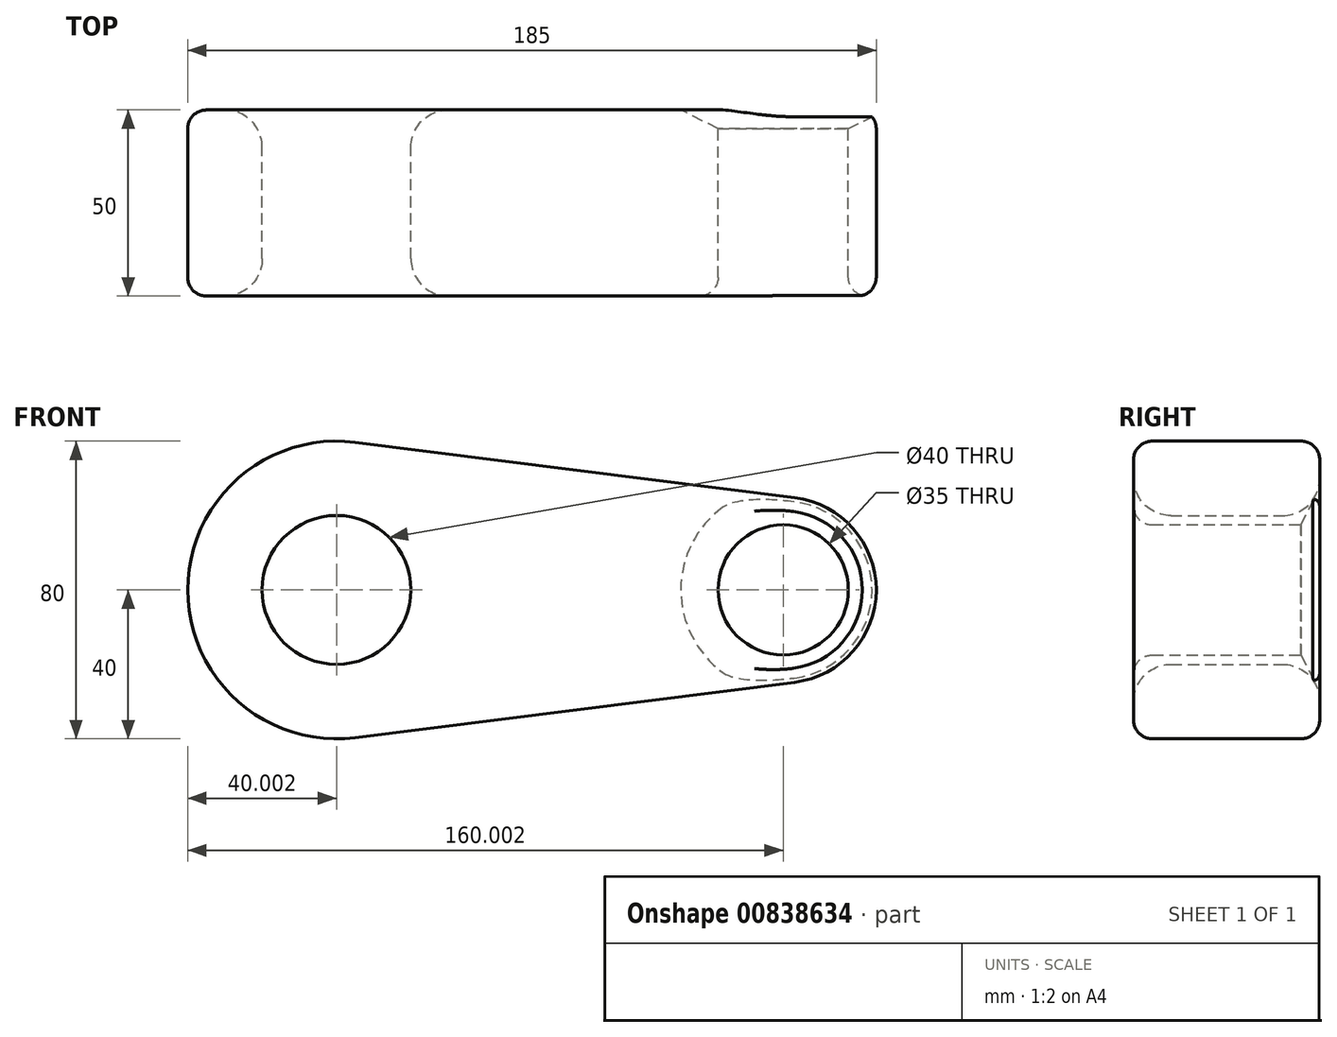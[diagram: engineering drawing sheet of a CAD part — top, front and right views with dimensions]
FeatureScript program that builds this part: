
annotation { "Feature Type Name" : "Feature", "Feature Type Description" : "" }
export const myFeature = defineFeature(function(context is Context, id is Id, definition is map)
    precondition{}
    {
        {
            var Q0;
            Q0=qCreatedBy(makeId("Front.planeOp"),FACE);
            var sketch = newSketch(context, id + "F0", { "sketchPlane" : qUnion([Q0])});
            skCircle(sketch, "E0", {"center": v(-83.9, 0) * mm, "radius": 40 * mm});
            skCircle(sketch, "E1", {"center": v(36.1, 0) * mm, "radius": 25 * mm});
            skLineSegment(sketch, "E2", {"start": v(-78.9, 39.69) * mm, "end": v(39.22, 24.8) * mm});
            skLineSegment(sketch, "E3", {"start": v(-78.9, -39.69) * mm, "end": v(39.22, -24.8) * mm});
            skCircle(sketch, "E4", {"center": v(-83.9, 0) * mm, "radius": 20 * mm});
            skCircle(sketch, "E5", {"center": v(36.1, 0) * mm, "radius": 17.5 * mm});
            skSolve(sketch);
        }
        {
            var Q0;
            Q0 = qSketchRegion(id + "F0", true);
            extrude(context, id + "F1", {"entities" : qUnion([Q0]), "depth" : 25 * mm, "offsetDistance" : 25 * mm});
        }
        {
            var Q0;
            Q0 = qSketchRegion(id + "F0", true);
            extrude(context, id + "F2", {"entities" : qUnion([Q0]), "operationType" : NewBodyOperationType.ADD, "depth" : 50 * mm, "offsetDistance" : 25 * mm});
        }
        {
            var Q0;
            {var subQ0=sQuery(id+"F0.wireOp",EDGE,"E4");Q0=makeQuery(id+"F2.boolean.opBoolean","MERGE",FACE,{"derivedFrom":[makeQuery(id+"F1.opExtrude","SWEPT_FACE",FACE,{"disambiguationData":[OSD([subQ0])]}),makeQuery(id+"F2.opExtrude","SWEPT_FACE",FACE,{"disambiguationData":[OSD([subQ0])]})]});}
            fillet(context, id + "F3", {"entities" : qUnion([Q0]), "radius" : 10 * mm, "tangentPropagation" : true, "allowEdgeOverflow" : false});
        }
        {
            var Q0;
            {var subQ0=sQuery(id+"F0.wireOp",EDGE,"E3");Q0=makeQuery(id+"F2.boolean.opBoolean","MERGE",FACE,{"derivedFrom":[makeQuery(id+"F1.opExtrude","SWEPT_FACE",FACE,{"disambiguationData":[OSD([subQ0])]}),makeQuery(id+"F2.opExtrude","SWEPT_FACE",FACE,{"disambiguationData":[OSD([subQ0])]})]});}
            var Q1;
            Q1=makeQuery(id+"F2.opExtrude","CAP_FACE",FACE,{"disambiguationData":[OSD([sQuery(id+"F0.wireOp",EDGE,"E0"),sQuery(id+"F0.wireOp",EDGE,"E1"),sQuery(id+"F0.wireOp",EDGE,"E2"),sQuery(id+"F0.wireOp",EDGE,"E3"),sQuery(id+"F0.wireOp",EDGE,"E4"),sQuery(id+"F0.wireOp",EDGE,"E5")])],"isStart":false});
            fillet(context, id + "F4", {"entities" : qUnion([Q0, Q1]), "radius" : 5 * mm, "tangentPropagation" : true, "allowEdgeOverflow" : false});
        }
        {
            var Q0;
            {var subQ0=sQuery(id+"F0.wireOp",EDGE,"E5");Q0=makeQuery(id+"F2.boolean.opBoolean","MERGE",FACE,{"derivedFrom":[makeQuery(id+"F1.opExtrude","SWEPT_FACE",FACE,{"disambiguationData":[OSD([subQ0])]}),makeQuery(id+"F2.opExtrude","SWEPT_FACE",FACE,{"disambiguationData":[OSD([subQ0])]})]});}
            var Q1;
            {var subQ0=sQuery(id+"F0.wireOp",EDGE,"E3");Q1=makeQuery(id+"F2.boolean.opBoolean","MERGE",FACE,{"derivedFrom":[makeQuery(id+"F1.opExtrude","SWEPT_FACE",FACE,{"disambiguationData":[OSD([subQ0])]}),makeQuery(id+"F2.opExtrude","SWEPT_FACE",FACE,{"disambiguationData":[OSD([subQ0])]})]});}
            var Q2;
            {var subQ0=sQuery(id+"F0.wireOp",EDGE,"E0");Q2=makeQuery(id+"F2.boolean.opBoolean","MERGE",FACE,{"derivedFrom":[makeQuery(id+"F1.opExtrude","SWEPT_FACE",FACE,{"disambiguationData":[OSD([subQ0])]}),makeQuery(id+"F2.opExtrude","SWEPT_FACE",FACE,{"disambiguationData":[OSD([subQ0])]})]});}
            var Q3;
            Q3=makeQuery(id+"F2.opExtrude","CAP_FACE",FACE,{"disambiguationData":[OSD([sQuery(id+"F0.wireOp",EDGE,"E0"),sQuery(id+"F0.wireOp",EDGE,"E1"),sQuery(id+"F0.wireOp",EDGE,"E2"),sQuery(id+"F0.wireOp",EDGE,"E3"),sQuery(id+"F0.wireOp",EDGE,"E4"),sQuery(id+"F0.wireOp",EDGE,"E5")])],"isStart":false});
            chamfer(context, id + "F5", {"entities" : qUnion([Q0, Q1, Q2, Q3]), "chamferType" : ChamferType.TWO_OFFSETS, "width1" : 5 * mm, "oppositeDirection" : true, "width2" : 10 * mm, "tangentPropagation" : true});
        }
    });
